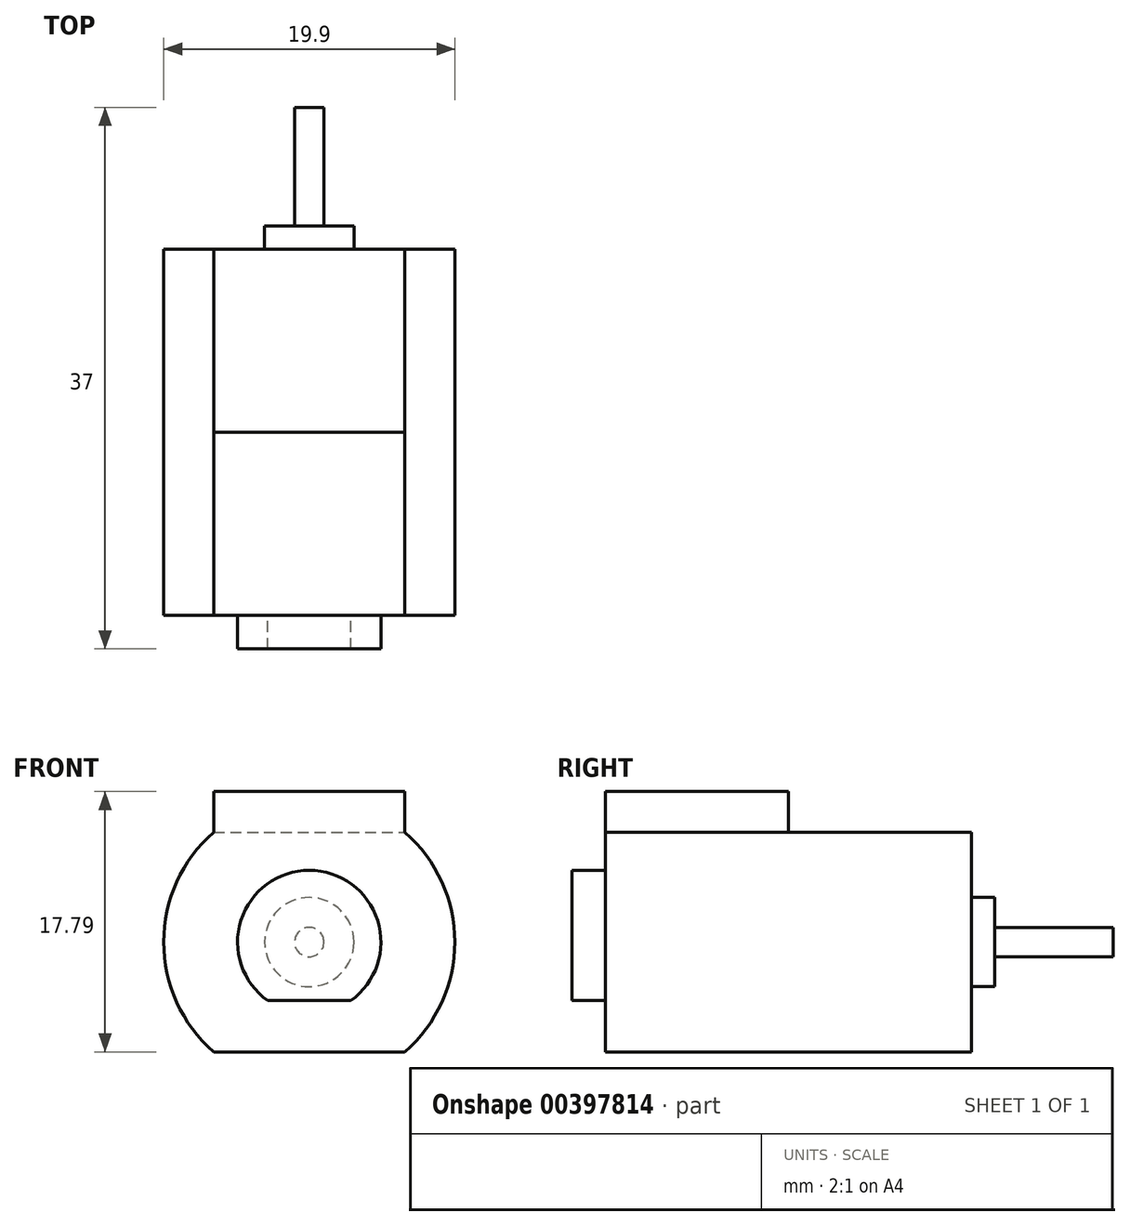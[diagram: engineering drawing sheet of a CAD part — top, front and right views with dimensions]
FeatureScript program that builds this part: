
annotation { "Feature Type Name" : "Feature", "Feature Type Description" : "" }
export const myFeature = defineFeature(function(context is Context, id is Id, definition is map)
    precondition{}
    {
        {
            var Q0;
            Q0=qCreatedBy(makeId("Front.planeOp"),FACE);
            var sketch = newSketch(context, id + "F0", { "sketchPlane" : qUnion([Q0])});
            skArc(sketch, "E0", {"start": v(-16.8, 20.56) * mm, "mid": v(-20.21, 13.06) * mm, "end": v(-16.8, 5.56) * mm});
            skLineSegment(sketch, "E1", {"start": v(-16.8, 20.56) * mm, "end": v(-3.72, 20.56) * mm});
            skLineSegment(sketch, "E2", {"start": v(-16.8, 5.56) * mm, "end": v(-3.72, 5.56) * mm});
            skArc(sketch, "E3.trimOffspring", {"start": v(-3.72, 5.56) * mm, "mid": v(-0.31, 13.06) * mm, "end": v(-3.72, 20.56) * mm});
            skCircle(sketch, "E4", {"center": v(-10.26, 13.06) * mm, "radius": 3.05 * mm});
            skCircle(sketch, "E5", {"center": v(-10.26, 13.06) * mm, "radius": 1 * mm});
            skArc(sketch, "E6", {"start": v(-7.43, 9.06) * mm, "mid": v(-10.26, 17.96) * mm, "end": v(-13.1, 9.06) * mm});
            skLineSegment(sketch, "E7", {"start": v(-13.1, 9.06) * mm, "end": v(-7.43, 9.06) * mm});
            skLineSegment(sketch, "E8", {"start": v(-3.72, 20.56) * mm, "end": v(-3.72, 23.35) * mm});
            skLineSegment(sketch, "E9", {"start": v(-3.72, 23.35) * mm, "end": v(-16.8, 23.35) * mm});
            skLineSegment(sketch, "E10", {"start": v(-16.8, 23.35) * mm, "end": v(-16.8, 20.56) * mm});
            skSolve(sketch);
        }
        {
            var Q0;
            Q0=makeQuery(id+"F0.imprint","IMPRINT",FACE,{"disambiguationData":[TD([[makeQuery(id+"F0.imprint","IMPRINT",EDGE,{"derivedFrom":sQuery(id+"F0.wireOp",EDGE,"E0")}),1.0]])]});
            var Q1;
            Q1=makeQuery(id+"F0.imprint","IMPRINT",FACE,{"disambiguationData":[TD([[makeQuery(id+"F0.imprint","IMPRINT",EDGE,{"derivedFrom":sQuery(id+"F0.wireOp",EDGE,"E4")}),1.0]])]});
            var Q2;
            Q2=makeQuery(id+"F0.imprint","IMPRINT",FACE,{"disambiguationData":[TD([[makeQuery(id+"F0.imprint","IMPRINT",EDGE,{"derivedFrom":sQuery(id+"F0.wireOp",EDGE,"E4")}),-1.0]])]});
            var Q3;
            Q3=makeQuery(id+"F0.imprint","IMPRINT",FACE,{"disambiguationData":[TD([[makeQuery(id+"F0.imprint","IMPRINT",EDGE,{"derivedFrom":sQuery(id+"F0.wireOp",EDGE,"E5")}),1.0]])]});
            extrude(context, id + "F1", {"entities" : qUnion([Q0, Q1, Q2, Q3]), "endBound" : BoundingType.SYMMETRIC, "depth" : 25 * mm});
        }
        {
            var Q0;
            Q0=makeQuery(id+"F0.imprint","IMPRINT",FACE,{"disambiguationData":[TD([[makeQuery(id+"F0.imprint","IMPRINT",EDGE,{"derivedFrom":sQuery(id+"F0.wireOp",EDGE,"E1")}),1.0]])]});
            extrude(context, id + "F2", {"entities" : qUnion([Q0]), "operationType" : NewBodyOperationType.ADD, "depth" : 12.5 * mm});
        }
        {
            var Q0;
            Q0=makeQuery(id+"F0.imprint","IMPRINT",FACE,{"disambiguationData":[TD([[makeQuery(id+"F0.imprint","IMPRINT",EDGE,{"derivedFrom":sQuery(id+"F0.wireOp",EDGE,"E4")}),-1.0]])]});
            var Q1;
            Q1=makeQuery(id+"F0.imprint","IMPRINT",FACE,{"disambiguationData":[TD([[makeQuery(id+"F0.imprint","IMPRINT",EDGE,{"derivedFrom":sQuery(id+"F0.wireOp",EDGE,"E4")}),1.0]])]});
            var Q2;
            Q2=makeQuery(id+"F0.imprint","IMPRINT",FACE,{"disambiguationData":[TD([[makeQuery(id+"F0.imprint","IMPRINT",EDGE,{"derivedFrom":sQuery(id+"F0.wireOp",EDGE,"E5")}),1.0]])]});
            extrude(context, id + "F3", {"entities" : qUnion([Q0, Q1, Q2]), "operationType" : NewBodyOperationType.ADD, "depth" : 14.8 * mm});
        }
        {
            var Q0;
            Q0=makeQuery(id+"F0.imprint","IMPRINT",FACE,{"disambiguationData":[TD([[makeQuery(id+"F0.imprint","IMPRINT",EDGE,{"derivedFrom":sQuery(id+"F0.wireOp",EDGE,"E4")}),1.0]])]});
            extrude(context, id + "F4", {"entities" : qUnion([Q0]), "operationType" : NewBodyOperationType.ADD, "oppositeDirection" : true, "depth" : 14.1 * mm});
        }
        {
            var Q0;
            Q0=makeQuery(id+"F0.imprint","IMPRINT",FACE,{"disambiguationData":[TD([[makeQuery(id+"F0.imprint","IMPRINT",EDGE,{"derivedFrom":sQuery(id+"F0.wireOp",EDGE,"E5")}),1.0]])]});
            extrude(context, id + "F5", {"entities" : qUnion([Q0]), "operationType" : NewBodyOperationType.ADD, "oppositeDirection" : true, "depth" : 22.2 * mm});
        }
    });
